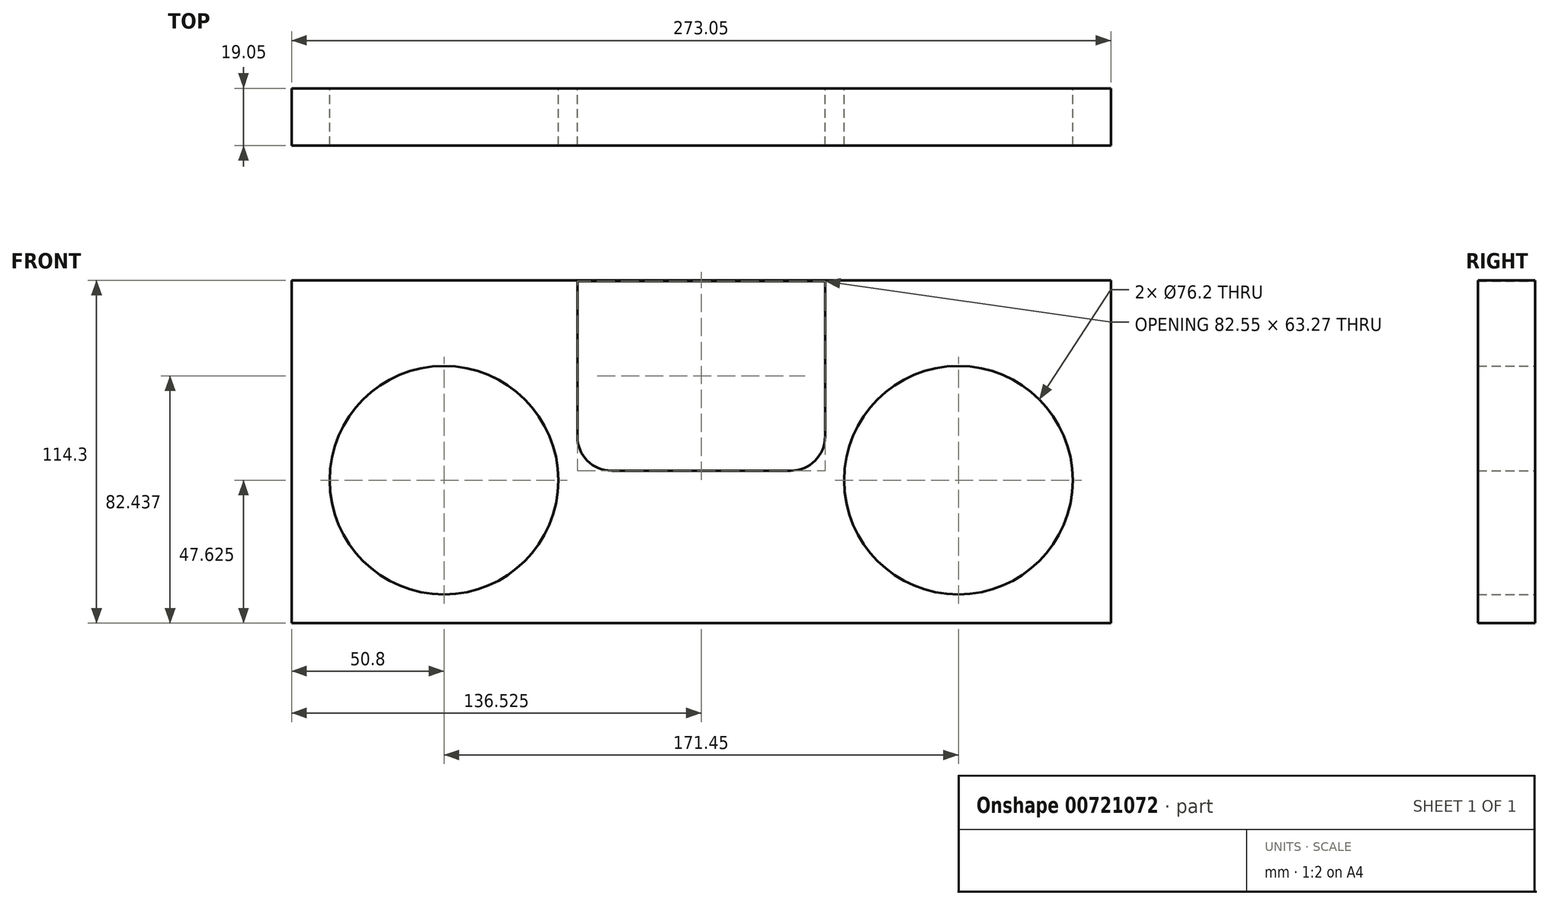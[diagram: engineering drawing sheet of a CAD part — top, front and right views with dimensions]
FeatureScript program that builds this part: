
annotation { "Feature Type Name" : "Feature", "Feature Type Description" : "" }
export const myFeature = defineFeature(function(context is Context, id is Id, definition is map)
    precondition{}
    {
        {
            var Q0;
            Q0=qCreatedBy(makeId("Front.planeOp"),FACE);
            var sketch = newSketch(context, id + "F0", { "sketchPlane" : qUnion([Q0])});
            skLineSegment(sketch, "E0.bottom", {"start": v(0, 0) * mm, "end": v(273.05, 0) * mm});
            skLineSegment(sketch, "E0.top", {"start": v(0, 114.3) * mm, "end": v(273.05, 114.3) * mm});
            skLineSegment(sketch, "E0.left", {"start": v(0, 0) * mm, "end": v(0, 114.3) * mm});
            skLineSegment(sketch, "E0.right", {"start": v(273.05, 0) * mm, "end": v(273.05, 114.3) * mm});
            skSolve(sketch);
        }
        {
            var Q0;
            Q0=qSketchRegion(id+"F0",true);
            extrude(context, id + "F1", {"entities" : qUnion([Q0]), "depth" : 19.05 * mm, "offsetDistance" : 25.4 * mm});
        }
        {
            var Q0;
            Q0=qCreatedBy(makeId("Front.planeOp"),FACE);
            var sketch = newSketch(context, id + "F2", { "sketchPlane" : qUnion([Q0])});
            skCircle(sketch, "E1", {"center": v(50.8, 47.63) * mm, "radius": 38.1 * mm});
            skCircle(sketch, "E2", {"center": v(222.25, 47.63) * mm, "radius": 38.1 * mm});
            skSolve(sketch);
        }
        {
            var Q0;
            Q0=makeQuery(id+"F2.imprint","IMPRINT",FACE,{"disambiguationData":[TD([[makeQuery(id+"F2.imprint","IMPRINT",EDGE,{"derivedFrom":sQuery(id+"F2.wireOp",EDGE,"E1")}),1.0]])]});
            var Q1;
            Q1=makeQuery(id+"F2.imprint","IMPRINT",FACE,{"disambiguationData":[TD([[makeQuery(id+"F2.imprint","IMPRINT",EDGE,{"derivedFrom":sQuery(id+"F2.wireOp",EDGE,"E2")}),1.0]])]});
            extrude(context, id + "F3", {"entities" : qUnion([Q0, Q1]), "operationType" : NewBodyOperationType.REMOVE, "depth" : 25.4 * mm, "offsetDistance" : 25.4 * mm});
        }
        {
            var Q0;
            Q0=qCreatedBy(makeId("Front.planeOp"),FACE);
            var sketch = newSketch(context, id + "F4", { "sketchPlane" : qUnion([Q0])});
            skLineSegment(sketch, "E3", {"start": v(95.25, 114.07) * mm, "end": v(95.25, 62.23) * mm});
            skLineSegment(sketch, "E4", {"start": v(106.68, 50.8) * mm, "end": v(166.37, 50.8) * mm});
            skLineSegment(sketch, "E5", {"start": v(177.8, 62.23) * mm, "end": v(177.8, 114.07) * mm});
            skPoint(sketch, "E6.visualSharp", {"position": v(95.25, 50.8) * mm});
            skArc(sketch, "E6.filletArc", {"start": v(95.25, 62.23) * mm, "mid": v(98.6, 54.15) * mm, "end": v(106.68, 50.8) * mm});
            skPoint(sketch, "E7.visualSharp", {"position": v(177.8, 50.8) * mm});
            skArc(sketch, "E7.filletArc", {"start": v(166.37, 50.8) * mm, "mid": v(174.45, 54.15) * mm, "end": v(177.8, 62.23) * mm});
            skLineSegment(sketch, "E8", {"start": v(95.25, 114.07) * mm, "end": v(177.8, 114.07) * mm});
            skSolve(sketch);
        }
        {
            var Q0;
            Q0=qSketchRegion(id+"F4",true);
            extrude(context, id + "F5", {"entities" : qUnion([Q0]), "operationType" : NewBodyOperationType.REMOVE, "oppositeDirection" : true, "depth" : 25.4 * mm, "offsetDistance" : 25.4 * mm});
        }
        {
            var Q0;
            Q0=qSketchRegion(id+"F4",true);
            extrude(context, id + "F6", {"entities" : qUnion([Q0]), "operationType" : NewBodyOperationType.REMOVE, "depth" : 25.4 * mm, "offsetDistance" : 25.4 * mm});
        }
        {
            var Q0;
            Q0 = qSketchRegion(id + "F4", true);
            extrude(context, id + "F7", {"entities" : qUnion([Q0]), "operationType" : NewBodyOperationType.REMOVE, "oppositeDirection" : true, "depth" : 25.4 * mm, "offsetDistance" : 25.4 * mm});
        }
    });
